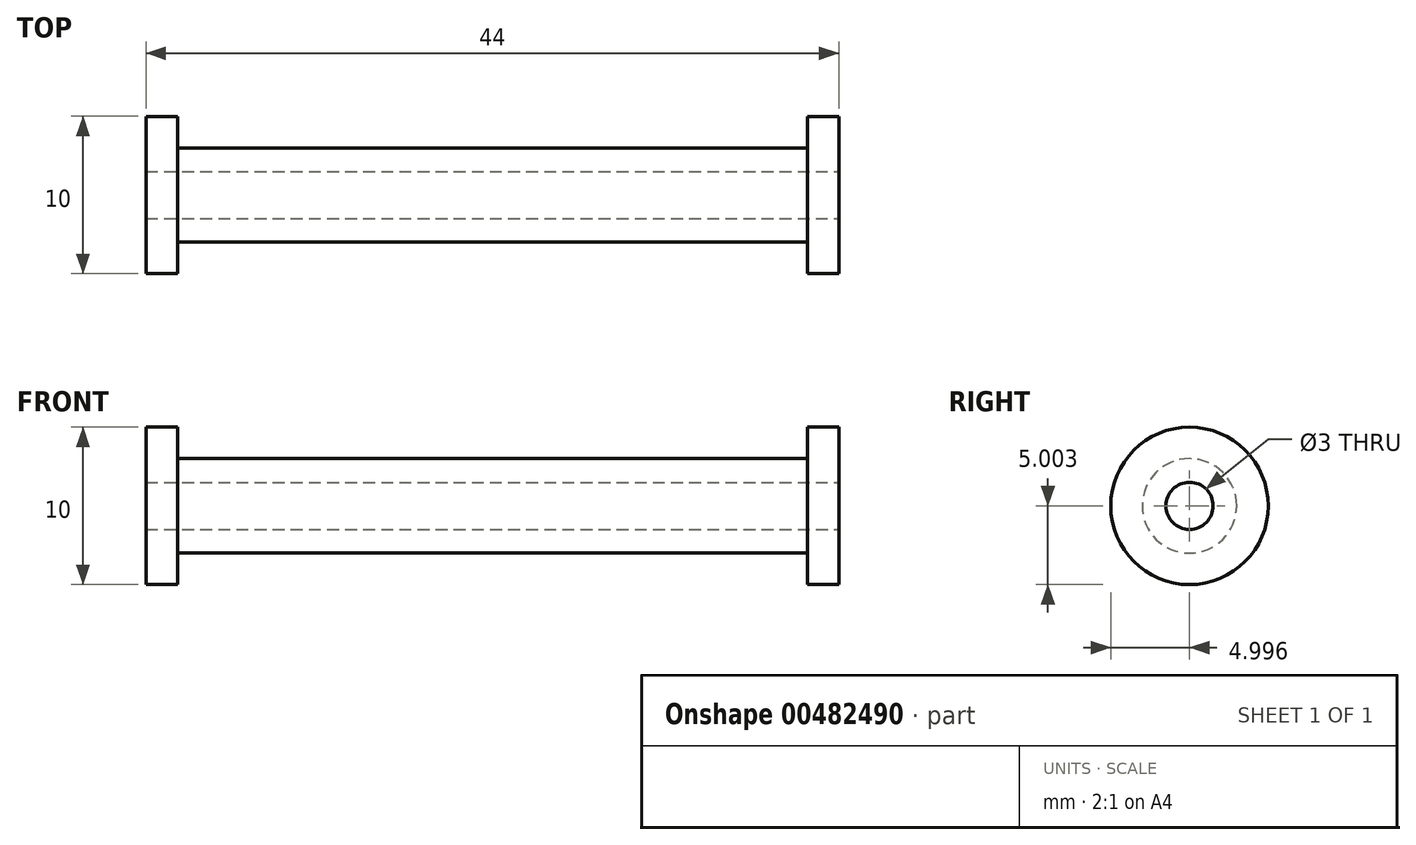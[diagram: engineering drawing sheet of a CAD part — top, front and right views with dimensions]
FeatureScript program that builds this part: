
annotation { "Feature Type Name" : "Feature", "Feature Type Description" : "" }
export const myFeature = defineFeature(function(context is Context, id is Id, definition is map)
    precondition{}
    {
        {
            var Q0;
            Q0=qCreatedBy(makeId("Right.planeOp"),FACE);
            var sketch = newSketch(context, id + "F0", { "sketchPlane" : qUnion([Q0])});
            skCircle(sketch, "E0", {"center": v(-6.2, 2.26) * mm, "radius": 3 * mm});
            skSolve(sketch);
        }
        {
            var Q0;
            Q0=makeQuery(id+"F0.imprint","IMPRINT",FACE,{"disambiguationData":[TD([[makeQuery(id+"F0.imprint","IMPRINT",EDGE,{"derivedFrom":sQuery(id+"F0.wireOp",EDGE,"E0")}),1.0]])]});
            extrude(context, id + "F1", {"entities" : qUnion([Q0]), "depth" : 40 * mm, "offsetDistance" : 25 * mm});
        }
        {
            var Q0;
            Q0=makeQuery(id+"F1.opExtrude","CAP_FACE",FACE,{"disambiguationData":[OSD([sQuery(id+"F0.wireOp",EDGE,"E0")])],"isStart":false});
            var sketch = newSketch(context, id + "F2", { "sketchPlane" : qUnion([Q0])});
            skCircle(sketch, "E1", {"center": v(-6.2, 2.26) * mm, "radius": 5 * mm});
            skSolve(sketch);
        }
        {
            var Q0;
            Q0=makeQuery(id+"F2.imprint","IMPRINT",FACE,{"disambiguationData":[TD([[makeQuery(id+"F2.imprint","IMPRINT",EDGE,{"derivedFrom":sQuery(id+"F2.wireOp",EDGE,"E1")}),1.0]])]});
            var Q1;
            Q1=makeQuery(id+"F2.imprint","IMPRINT",FACE,{"disambiguationData":[TD([[makeQuery(id+"F2.imprint","IMPRINT",EDGE,{"derivedFrom":makeQuery(id+"F1.opExtrude","CAP_EDGE",EDGE,{"disambiguationData":[OSD([sQuery(id+"F0.wireOp",EDGE,"E0")])],"isStart":false})}),1.0]])]});
            extrude(context, id + "F3", {"entities" : qUnion([Q0, Q1]), "operationType" : NewBodyOperationType.ADD, "depth" : 2 * mm, "offsetDistance" : 25 * mm});
        }
        {
            var Q0;
            Q0=makeQuery(id+"F1.opExtrude","CAP_FACE",FACE,{"disambiguationData":[OSD([sQuery(id+"F0.wireOp",EDGE,"E0")])],"isStart":true});
            var sketch = newSketch(context, id + "F4", { "sketchPlane" : qUnion([Q0])});
            skCircle(sketch, "E2", {"center": v(6.2, 2.26) * mm, "radius": 5 * mm});
            skSolve(sketch);
        }
        {
            var Q0;
            Q0=makeQuery(id+"F4.imprint","IMPRINT",FACE,{"disambiguationData":[TD([[makeQuery(id+"F4.imprint","IMPRINT",EDGE,{"derivedFrom":sQuery(id+"F4.wireOp",EDGE,"E2")}),1.0]])]});
            var Q1;
            Q1=makeQuery(id+"F4.imprint","IMPRINT",FACE,{"disambiguationData":[TD([[makeQuery(id+"F4.imprint","IMPRINT",EDGE,{"derivedFrom":makeQuery(id+"F1.opExtrude","CAP_EDGE",EDGE,{"disambiguationData":[OSD([sQuery(id+"F0.wireOp",EDGE,"E0")])],"isStart":true})}),-1.0]])]});
            extrude(context, id + "F5", {"entities" : qUnion([Q0, Q1]), "operationType" : NewBodyOperationType.ADD, "depth" : 2 * mm, "offsetDistance" : 25 * mm});
        }
        {
            var Q0;
            Q0=makeQuery(id+"F3.opExtrude","CAP_FACE",FACE,{"disambiguationData":[OSD([sQuery(id+"F2.wireOp",EDGE,"E1")])],"isStart":false});
            var sketch = newSketch(context, id + "F6", { "sketchPlane" : qUnion([Q0])});
            skCircle(sketch, "E3", {"center": v(-6.2, 2.26) * mm, "radius": 1.5 * mm});
            skSolve(sketch);
        }
        {
            var Q0;
            Q0=makeQuery(id+"F6.imprint","IMPRINT",FACE,{"disambiguationData":[TD([[makeQuery(id+"F6.imprint","IMPRINT",EDGE,{"derivedFrom":sQuery(id+"F6.wireOp",EDGE,"E3")}),1.0]])]});
            extrude(context, id + "F7", {"entities" : qUnion([Q0]), "operationType" : NewBodyOperationType.REMOVE, "oppositeDirection" : true, "depth" : 44 * mm, "offsetDistance" : 25 * mm});
        }
    });
